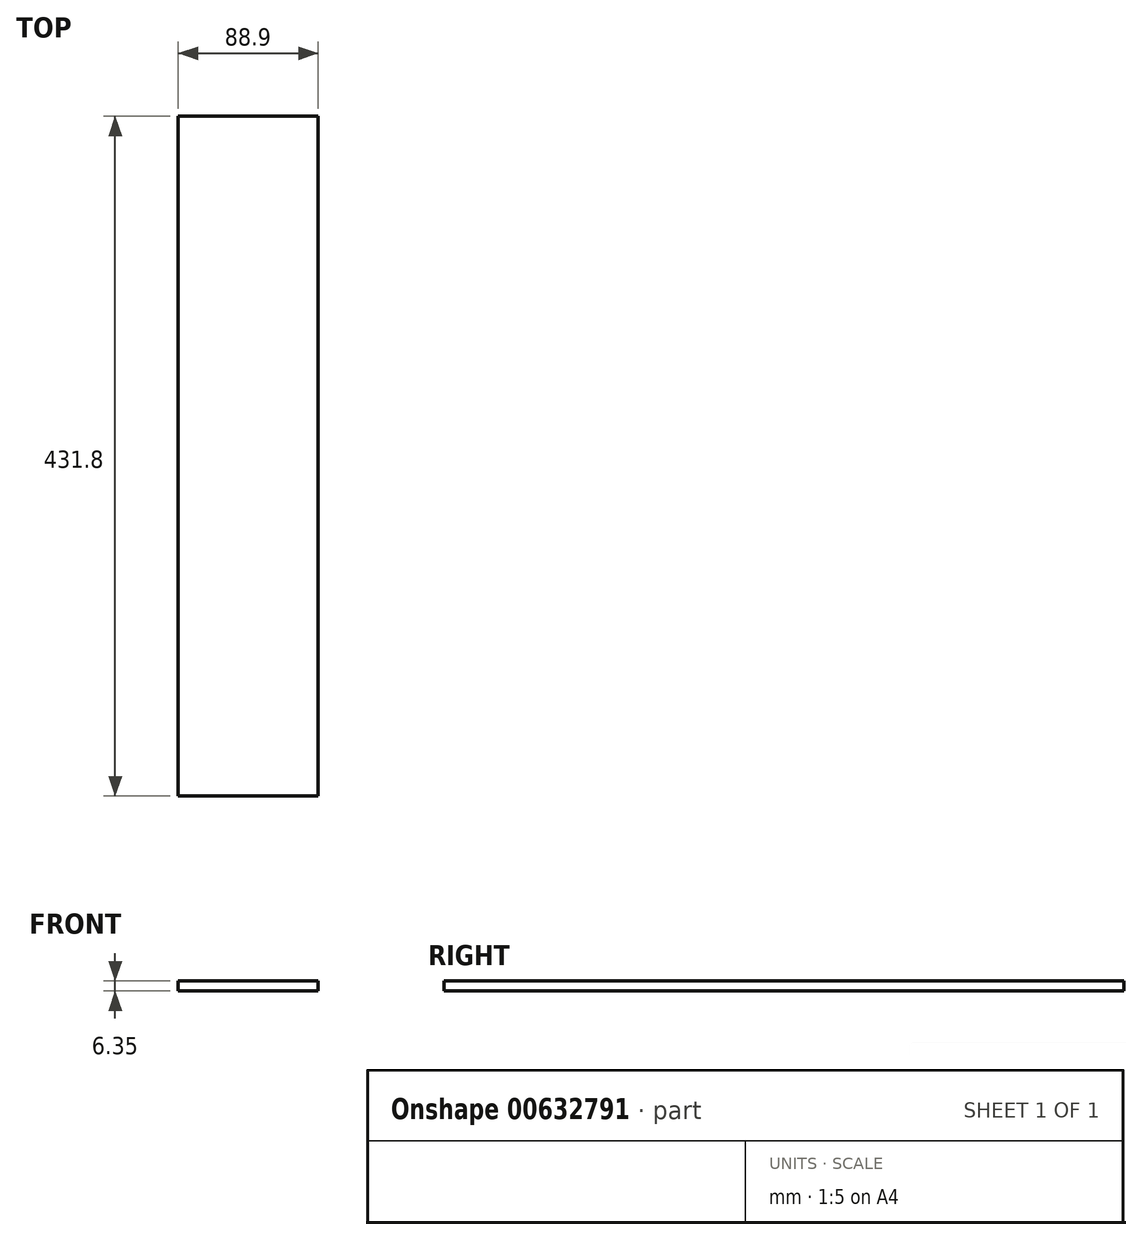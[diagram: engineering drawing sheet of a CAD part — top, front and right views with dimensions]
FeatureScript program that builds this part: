
annotation { "Feature Type Name" : "Feature", "Feature Type Description" : "" }
export const myFeature = defineFeature(function(context is Context, id is Id, definition is map)
    precondition{}
    {
        {
            var Q0;
            Q0=qCreatedBy(makeId("Top.planeOp"),FACE);
            var sketch = newSketch(context, id + "F0", { "sketchPlane" : qUnion([Q0])});
            skLineSegment(sketch, "E0.bottom", {"start": v(0, 0) * mm, "end": v(88.9, 0) * mm});
            skLineSegment(sketch, "E0.top", {"start": v(0, 431.8) * mm, "end": v(88.9, 431.8) * mm});
            skLineSegment(sketch, "E0.left", {"start": v(0, 0) * mm, "end": v(0, 431.8) * mm});
            skLineSegment(sketch, "E0.right", {"start": v(88.9, 0) * mm, "end": v(88.9, 431.8) * mm});
            skSolve(sketch);
        }
        {
            var Q0;
            Q0 = qSketchRegion(id + "F0", true);
            extrude(context, id + "F1", {"entities" : qUnion([Q0]), "depth" : 6.35 * mm, "offsetDistance" : 25.4 * mm});
        }
    });
